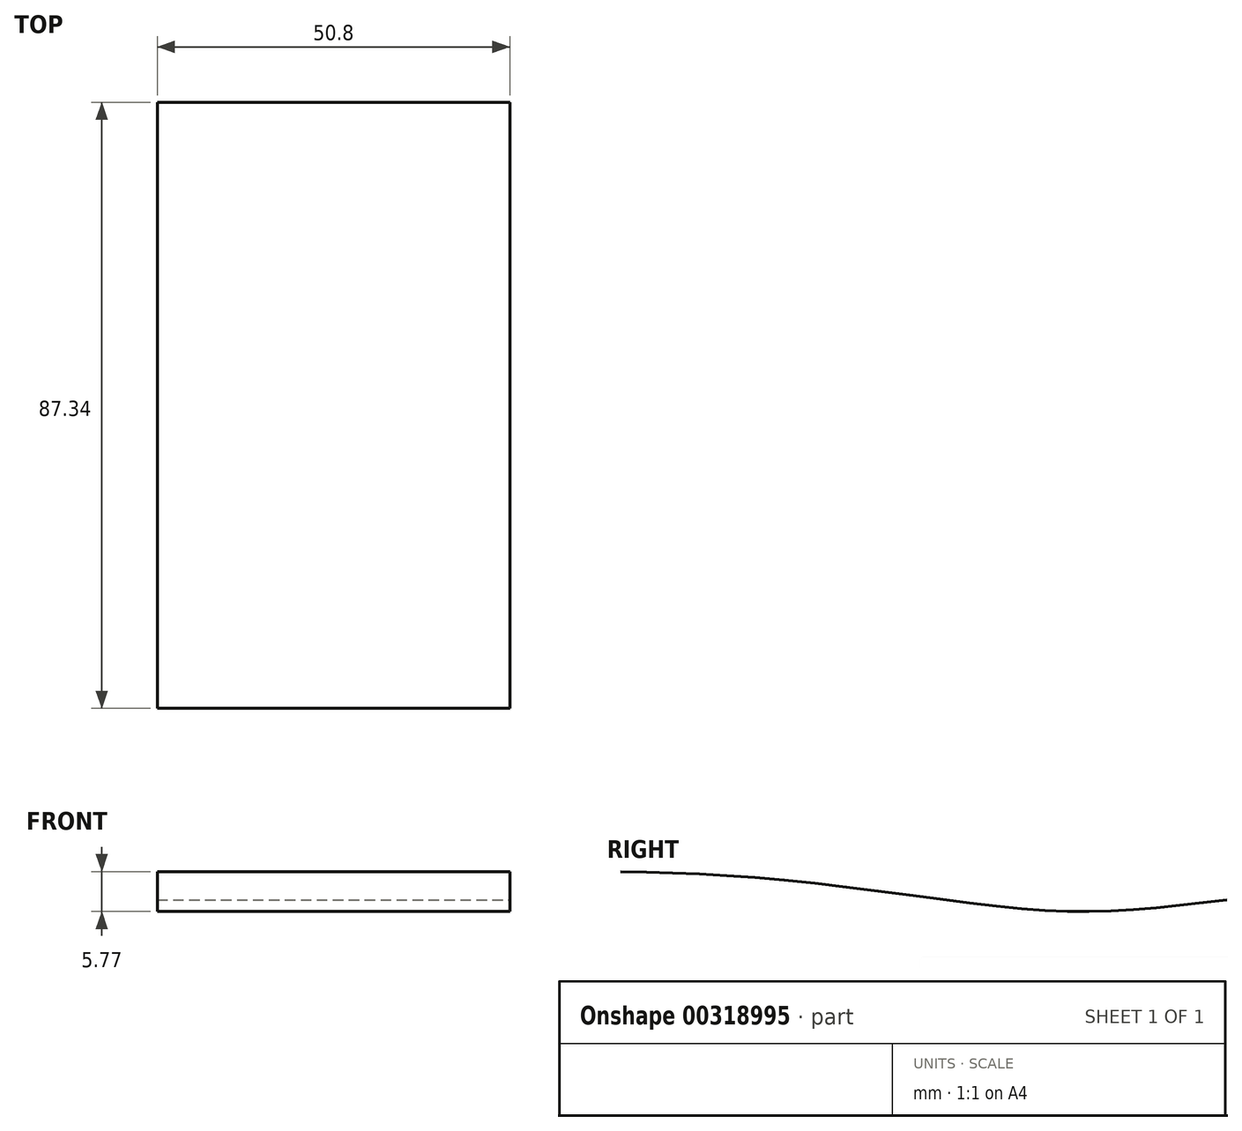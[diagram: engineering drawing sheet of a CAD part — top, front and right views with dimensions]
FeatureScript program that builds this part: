
annotation { "Feature Type Name" : "Feature", "Feature Type Description" : "" }
export const myFeature = defineFeature(function(context is Context, id is Id, definition is map)
    precondition{}
    {
        {
            var Q0;
            Q0=qCreatedBy(makeId("Right.planeOp"),FACE);
            var sketch = newSketch(context, id + "F0", { "sketchPlane" : qUnion([Q0])});
            skFitSpline(sketch, "E0", {"points": [v(-4.68, 9.37) * mm, v(18.93, 8.14) * mm, v(48.66, 4.48) * mm, v(65.56, 3.66) * mm, v(82.66, 5.3) * mm], "startDerivative": vector(85.66, -2.22) * mm, "endDerivative": vector(78.5, 9.56) * mm});
            skSolve(sketch);
        }
        {
            var Q0;
            Q0=sQuery(id+"F0.wireOp",EDGE,"E0");
            extrude(context, id + "F1", {"bodyType" : ToolBodyType.SURFACE, "surfaceEntities" : qUnion([Q0]), "depth" : 25.4 * mm, "hasSecondDirection" : true, "secondDirectionOppositeDirection" : true, "secondDirectionDepth" : 25.4 * mm});
        }
    });
